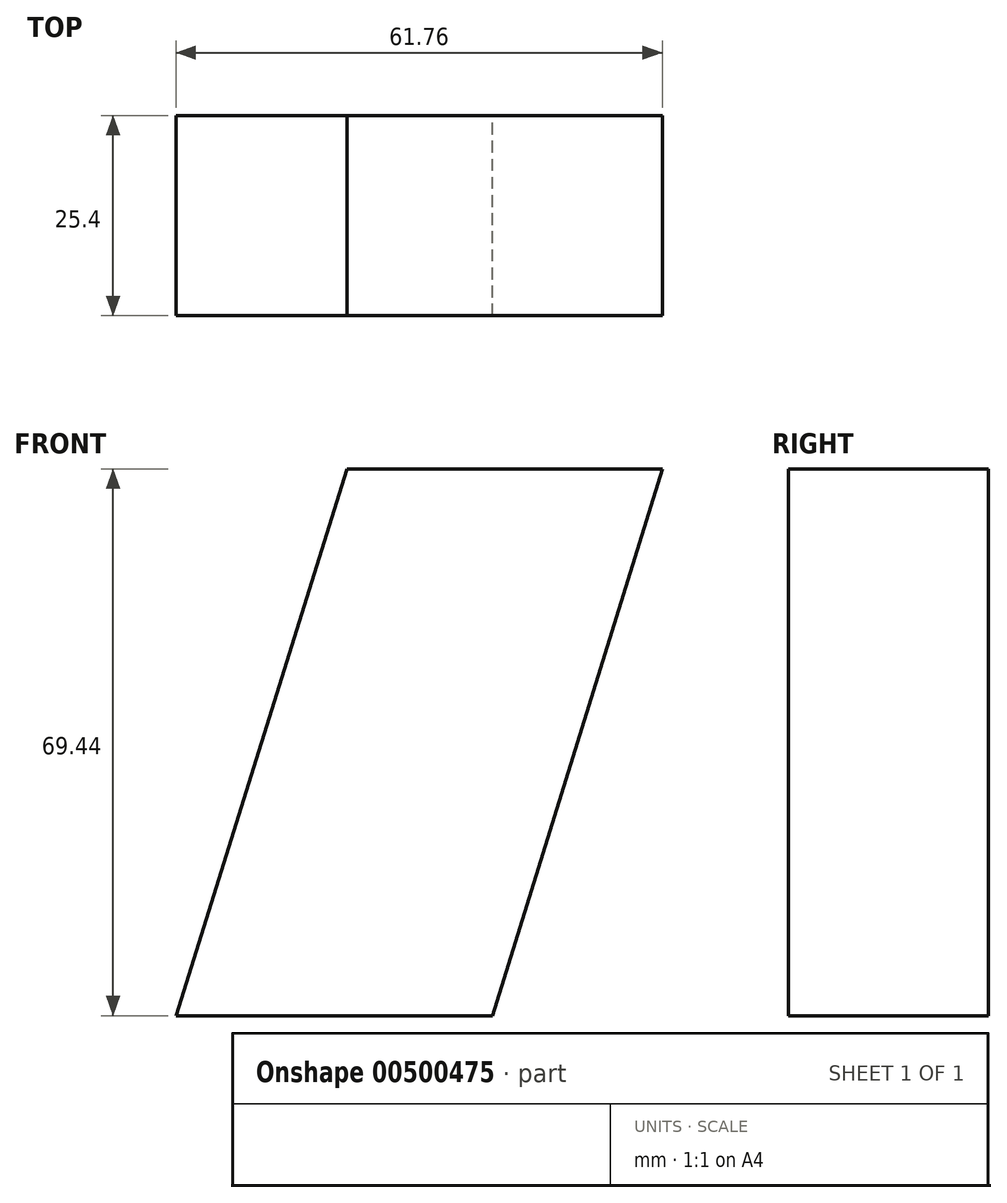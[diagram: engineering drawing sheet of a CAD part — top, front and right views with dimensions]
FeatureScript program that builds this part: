
annotation { "Feature Type Name" : "Feature", "Feature Type Description" : "" }
export const myFeature = defineFeature(function(context is Context, id is Id, definition is map)
    precondition{}
    {
        {
            var Q0;
            Q0=qCreatedBy(makeId("Front.planeOp"),FACE);
            var sketch = newSketch(context, id + "F0", { "sketchPlane" : qUnion([Q0])});
            skLineSegment(sketch, "E0", {"start": v(-61.57, 37.77) * mm, "end": v(-21.56, 37.77) * mm});
            skLineSegment(sketch, "E1", {"start": v(-21.56, 37.77) * mm, "end": v(-43.15, -31.67) * mm});
            skLineSegment(sketch, "E2", {"start": v(-43.15, -31.67) * mm, "end": v(-83.32, -31.67) * mm});
            skLineSegment(sketch, "E3", {"start": v(-83.32, -31.67) * mm, "end": v(-61.57, 37.77) * mm});
            skSolve(sketch);
        }
        {
            var Q0;
            Q0 = qSketchRegion(id + "F0", true);
            extrude(context, id + "F1", {"entities" : qUnion([Q0]), "depth" : 25.4 * mm});
        }
    });
